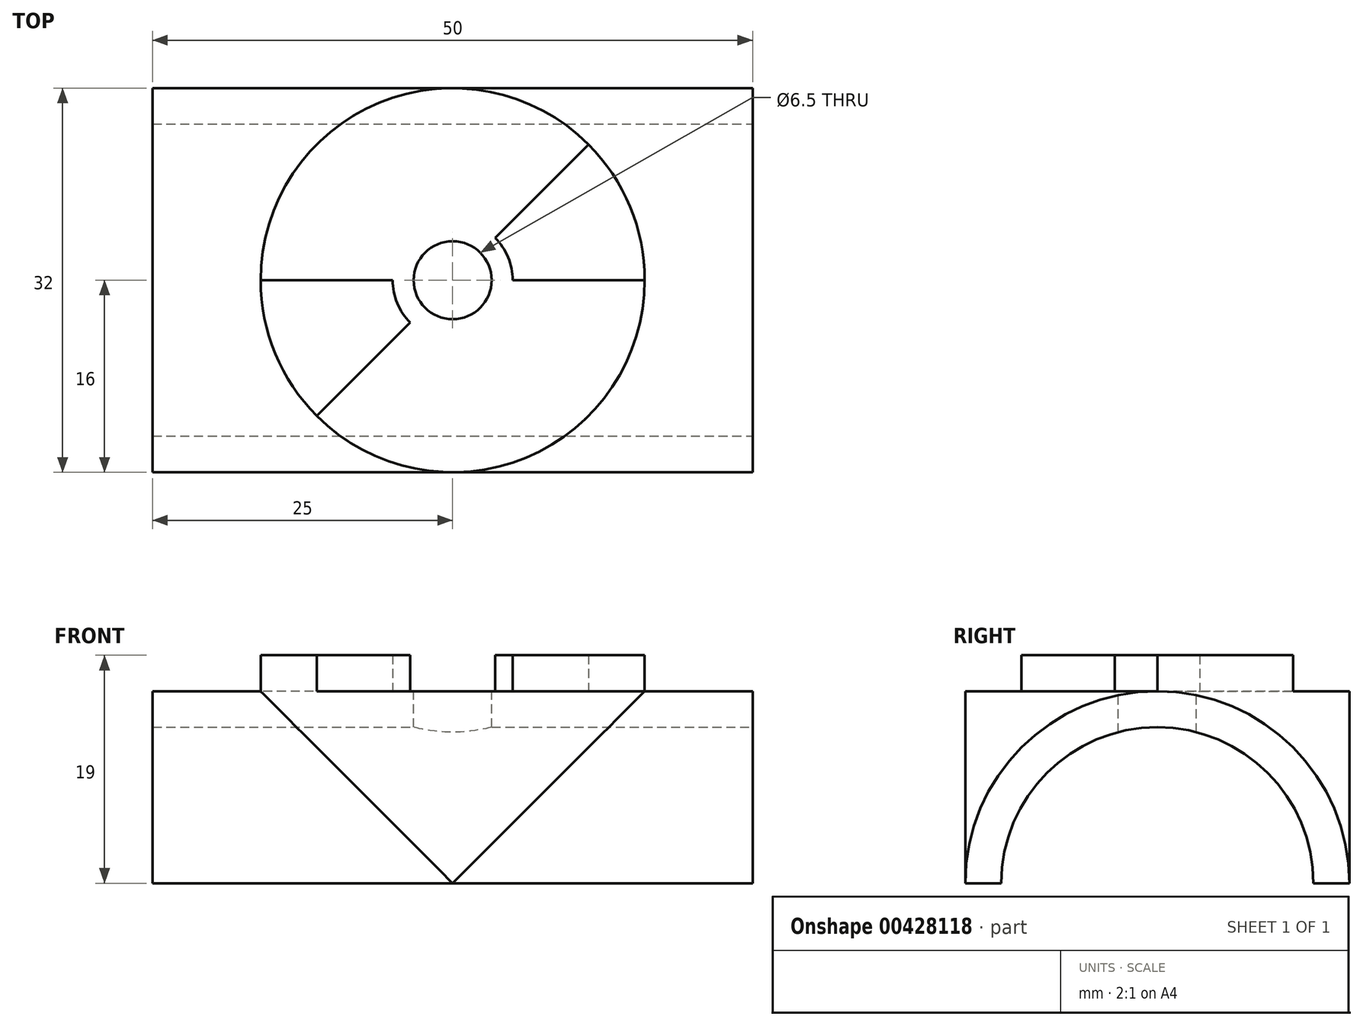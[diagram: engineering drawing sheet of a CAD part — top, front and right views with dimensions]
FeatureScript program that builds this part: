
annotation { "Feature Type Name" : "Feature", "Feature Type Description" : "" }
export const myFeature = defineFeature(function(context is Context, id is Id, definition is map)
    precondition{}
    {
        {
            var Q0;
            Q0=qCreatedBy(makeId("Right.planeOp"),FACE);
            var sketch = newSketch(context, id + "F0", { "sketchPlane" : qUnion([Q0])});
            skArc(sketch, "E0.0", {"start": v(16, 0) * mm, "mid": v(0, 16) * mm, "end": v(-16, 0) * mm});
            skLineSegment(sketch, "E1", {"start": v(-16, 0) * mm, "end": v(16, 0) * mm});
            skSolve(sketch);
        }
        {
            var Q0;
            Q0 = qSketchRegion(id + "F0", true);
            extrude(context, id + "F1", {"entities" : qUnion([Q0]), "endBound" : BoundingType.SYMMETRIC, "depth" : 50 * mm});
        }
        {
            var Q0;
            Q0=qCreatedBy(makeId("Top.planeOp"),FACE);
            var sketch = newSketch(context, id + "F2", { "sketchPlane" : qUnion([Q0])});
            skCircle(sketch, "E2", {"center": v(0, 0) * mm, "radius": 16 * mm});
            skSolve(sketch);
        }
        {
            var Q0;
            Q0 = qSketchRegion(id + "F2", true);
            extrude(context, id + "F3", {"entities" : qUnion([Q0]), "operationType" : NewBodyOperationType.ADD, "depth" : 16 * mm});
        }
        {
            var Q0;
            Q0=makeQuery(id+"F3.opExtrude","CAP_FACE",FACE,{"disambiguationData":[OSD([sQuery(id+"F2.wireOp",EDGE,"E2")])],"isStart":false});
            var sketch = newSketch(context, id + "F4", { "sketchPlane" : qUnion([Q0])});
            skArc(sketch, "E3.0", {"start": v(-16, 0) * mm, "mid": v(-14.78, -6.12) * mm, "end": v(-11.31, -11.31) * mm});
            skArc(sketch, "E3.1", {"start": v(16, 0) * mm, "mid": v(14.78, 6.12) * mm, "end": v(11.31, 11.31) * mm});
            skLineSegment(sketch, "E4", {"start": v(-5, 0) * mm, "end": v(-16, 0) * mm});
            skLineSegment(sketch, "E5", {"start": v(5, 0) * mm, "end": v(16, 0) * mm});
            skLineSegment(sketch, "E6", {"start": v(-11.31, -11.31) * mm, "end": v(-3.54, -3.54) * mm});
            skLineSegment(sketch, "E7.trimOffspring", {"start": v(3.54, 3.54) * mm, "end": v(11.31, 11.31) * mm});
            skArc(sketch, "E8", {"start": v(-5, 0) * mm, "mid": v(-4.62, -1.91) * mm, "end": v(-3.54, -3.54) * mm});
            skArc(sketch, "E9.trimOffspring", {"start": v(5, 0) * mm, "mid": v(4.62, 1.91) * mm, "end": v(3.54, 3.54) * mm});
            skSolve(sketch);
        }
        {
            var Q0;
            Q0 = qSketchRegion(id + "F4", true);
            extrude(context, id + "F5", {"entities" : qUnion([Q0]), "operationType" : NewBodyOperationType.ADD, "depth" : 3 * mm});
        }
        {
            var Q0;
            Q0=makeQuery(id+"F3.opExtrude","CAP_FACE",FACE,{"disambiguationData":[OSD([sQuery(id+"F2.wireOp",EDGE,"E2")])],"isStart":false});
            var sketch = newSketch(context, id + "F6", { "sketchPlane" : qUnion([Q0])});
            skCircle(sketch, "E10", {"center": v(0, 0) * mm, "radius": 3.25 * mm});
            skSolve(sketch);
        }
        {
            var Q0;
            Q0 = qSketchRegion(id + "F6", true);
            extrude(context, id + "F7", {"entities" : qUnion([Q0]), "operationType" : NewBodyOperationType.REMOVE, "oppositeDirection" : true, "depth" : 25 * mm});
        }
        {
            var Q0;
            Q0=makeQuery(id+"F1.opExtrude","CAP_FACE",FACE,{"disambiguationData":[OSD([sQuery(id+"F0.wireOp",EDGE,"E0.0"),sQuery(id+"F0.wireOp",EDGE,"E1")])],"isStart":false});
            var sketch = newSketch(context, id + "F8", { "sketchPlane" : qUnion([Q0])});
            skArc(sketch, "E11", {"start": v(13, 0) * mm, "mid": v(0, 13) * mm, "end": v(-13, 0) * mm});
            skLineSegment(sketch, "E12", {"start": v(-13, 0) * mm, "end": v(13, 0) * mm});
            skSolve(sketch);
        }
        {
            var Q0;
            Q0 = qSketchRegion(id + "F8", true);
            extrude(context, id + "F9", {"entities" : qUnion([Q0]), "operationType" : NewBodyOperationType.REMOVE, "endBound" : BoundingType.THROUGH_ALL, "oppositeDirection" : true, "depth" : 25 * mm});
        }
    });
